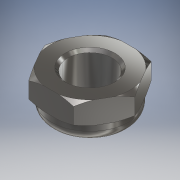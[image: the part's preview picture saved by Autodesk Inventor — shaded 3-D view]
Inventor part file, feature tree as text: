
AUTODESK INVENTOR PART (.ipt)
format: ipt  version: 2019 (Build 230136000, 136)  size: 229,888 bytes
history: native  units: mm
features: sketch x4, extrude x3, fillet x2, other x1, revolve x1, chamfer x1
ambient origin geometry x8: Origin, YZ Plane, XZ Plane, XY Plane, X Axis, Y Axis, Z Axis, Center Point
bodies: Body1 (feature_tree)
feature tree (12):
  other  "Твердое тело1"
  extrude  "Выдавливание1"  Depth=8.0mm
  revolve  "Вращение1"
  extrude  "Выдавливание2"  Depth=14.0mm
  fillet  "Сопряжение1"  Radius=4.0mm
  extrude  "Выдавливание3"  TaperAngle=60.0deg  [1 undecoded]
  fillet  "Сопряжение2"  Radius=1.0mm
  chamfer  "Фаска2"  Distance=3.5mm
  sketch  "Эскиз1"
  sketch  "Эскиз2"
  sketch  "Эскиз3"
  sketch  "Эскиз4"
note: 1 required parameter value undecoded (feature->parameter linkage not recoverable at this tier; creation-order binding heuristic only, values carry confidence <= 0.55)
